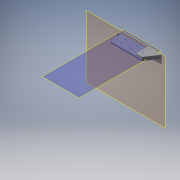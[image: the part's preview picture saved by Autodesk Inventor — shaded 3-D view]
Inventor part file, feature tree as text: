
AUTODESK INVENTOR PART (.ipt)
format: ipt  version: 2016 (Build 200138000, 138)  size: 215,040 bytes
history: native  units: in
note: dims shown in document units (in); Inventor stores cm internally (conversion verified against a paired STEP export)
features: extrude x9, sketch x9, reference x8, plane x7, projected_geometry x5, chamfer x1
ambient origin geometry x8: Origin, YZ Plane, XZ Plane, XY Plane, X Axis, Y Axis, Z Axis, Center Point
bodies: Solid1 (feature_tree)
feature tree (39):
  plane  "Work Plane1"
  extrude  "Extrusion1"  Depth=0.2in
  plane  "Work Plane2"
  extrude  "Extrusion2"  Depth=1.0in TaperAngle=0.0deg
  extrude  "Extrusion3"  Depth=2.5in
  sketch  "Sketch4"  dims[d10=0.2in d11=0.0in d12=0.2in d13=0.0in]
  plane  "Work Plane3"
  extrude  "Extrusion4"  Depth=0.2in TaperAngle=0.0deg
  extrude  "Extrusion5"  Depth=0.2in TaperAngle=0.0deg
  plane  "Work Plane4"
  extrude  "Extrusion6"  Depth=1.5625in
  plane  "Work Plane6"
  extrude  "Extrusion7"  Depth=0.2in TaperAngle=45.0deg
  extrude  "Extrusion8"  [1 undecoded]
  plane  "Work Plane7"
  extrude  "Extrusion9"  [1 undecoded]
  chamfer  "Chamfer1"  [1 undecoded]
  sketch  "Sketch1"  dims[d0=0.2in d1=0.0in d2=0.75in]
  reference  "Reference1"
  reference  "Reference2"
  reference  "Reference3"
  reference  "Reference4"
  sketch  "Sketch2"  dims[d3=0.2in d4=0.0in d5=1.0in d6=0.0in]
  reference  "Reference5"
  sketch  "Sketch3"  dims[d7=0.2in d8=0.0in d9=2.5in]
  reference  "Reference6"
  projected_geometry  "Projected Loop1"
  sketch  "Sketch5"  dims[d14=1.625in d15=2.25in d16=0.2in d17=0.0in]
  projected_geometry  "Projected Loop2"
  reference  "Reference7"
  reference  "Reference8"
  sketch  "Sketch6"  dims[d18=0.2in d19=0.0in d20=1.5625in]
  plane  "Work Plane5"
  sketch  "Sketch7"  dims[d21=0.2in d22=0.0in d23=0.875in d24=0.125in d25=45.0deg]
  projected_geometry  "Projected Loop3"
  sketch  "Sketch8"
  projected_geometry  "Projected Loop4"
  sketch  "Sketch9"
  projected_geometry  "Projected Loop5"
note: 3 required parameter values undecoded (feature->parameter linkage not recoverable at this tier; creation-order binding heuristic only, values carry confidence <= 0.55)
